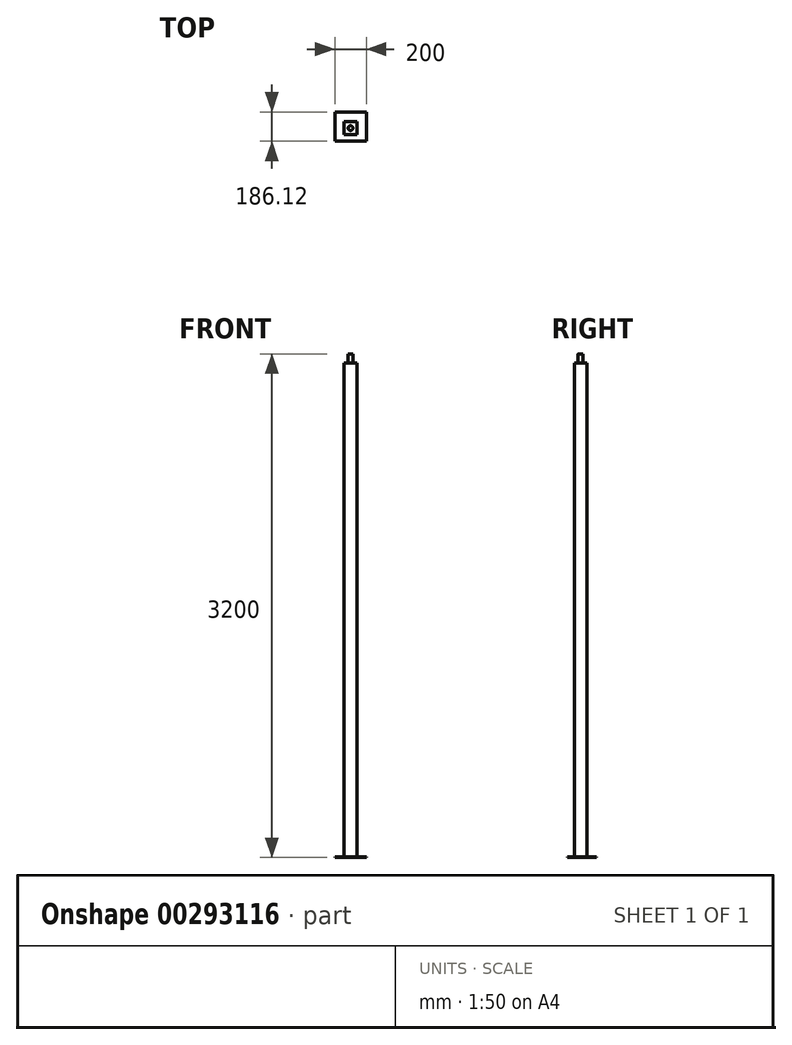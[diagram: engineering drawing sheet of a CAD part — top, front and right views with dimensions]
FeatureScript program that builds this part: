
annotation { "Feature Type Name" : "Feature", "Feature Type Description" : "" }
export const myFeature = defineFeature(function(context is Context, id is Id, definition is map)
    precondition{}
    {
        {
            var Q0;
            Q0=qCreatedBy(makeId("Top.planeOp"),FACE);
            var sketch = newSketch(context, id + "F0", { "sketchPlane" : qUnion([Q0])});
            skLineSegment(sketch, "E0.bottom", {"start": v(100, -93.06) * mm, "end": v(-100, -93.06) * mm});
            skLineSegment(sketch, "E0.top", {"start": v(100, 93.06) * mm, "end": v(-100, 93.06) * mm});
            skLineSegment(sketch, "E0.left", {"start": v(100, -93.06) * mm, "end": v(100, 93.06) * mm});
            skLineSegment(sketch, "E0.right", {"start": v(-100, -93.06) * mm, "end": v(-100, 93.06) * mm});
            skPoint(sketch, "E0.middle", {"position": v(0, 0) * mm});
            skSolve(sketch);
        }
        {
            var Q0;
            Q0=makeQuery(id+"F0.imprint","IMPRINT",FACE,{"disambiguationData":[TD([[makeQuery(id+"F0.imprint","IMPRINT",EDGE,{"derivedFrom":sQuery(id+"F0.wireOp",EDGE,"E0.bottom")}),-1.0]])]});
            extrude(context, id + "F1", {"entities" : qUnion([Q0]), "depth" : 3 * mm});
        }
        {
            var Q0;
            Q0=makeQuery(id+"F1.opExtrude","CAP_FACE",FACE,{"disambiguationData":[OSD([sQuery(id+"F0.wireOp",EDGE,"E0.bottom"),sQuery(id+"F0.wireOp",EDGE,"E0.top"),sQuery(id+"F0.wireOp",EDGE,"E0.left"),sQuery(id+"F0.wireOp",EDGE,"E0.right")])],"isStart":false});
            var sketch = newSketch(context, id + "F2", { "sketchPlane" : qUnion([Q0])});
            skLineSegment(sketch, "E1.bottom", {"start": v(40, -49.32) * mm, "end": v(-40, -49.32) * mm});
            skLineSegment(sketch, "E1.top", {"start": v(40, 30.68) * mm, "end": v(-40, 30.68) * mm});
            skLineSegment(sketch, "E1.left", {"start": v(40, -49.32) * mm, "end": v(40, 30.68) * mm});
            skLineSegment(sketch, "E1.right", {"start": v(-40, -49.32) * mm, "end": v(-40, 30.68) * mm});
            skPoint(sketch, "E1.middle", {"position": v(0, -9.32) * mm});
            skSolve(sketch);
        }
        {
            var Q0;
            Q0=makeQuery(id+"F2.imprint","IMPRINT",FACE,{"disambiguationData":[TD([[makeQuery(id+"F2.imprint","IMPRINT",EDGE,{"derivedFrom":sQuery(id+"F2.wireOp",EDGE,"E1.bottom")}),-1.0]])]});
            extrude(context, id + "F3", {"entities" : qUnion([Q0]), "operationType" : NewBodyOperationType.ADD, "depth" : 3197 * mm});
        }
        {
            var Q0;
            Q0=makeQuery(id+"F3.opExtrude","CAP_FACE",FACE,{"disambiguationData":[OSD([sQuery(id+"F2.wireOp",EDGE,"E1.bottom"),sQuery(id+"F2.wireOp",EDGE,"E1.top"),sQuery(id+"F2.wireOp",EDGE,"E1.left"),sQuery(id+"F2.wireOp",EDGE,"E1.right")])],"isStart":false});
            var sketch = newSketch(context, id + "F4", { "sketchPlane" : qUnion([Q0])});
            skCircle(sketch, "E2", {"center": v(0, -9.32) * mm, "radius": 15 * mm});
            skPoint(sketch, "E2.centerSnap0", {"position": v(40, -9.32) * mm});
            skSolve(sketch);
        }
        {
            var Q0;
            Q0=makeQuery(id+"F4.imprint","IMPRINT",FACE,{"disambiguationData":[TD([[makeQuery(id+"F4.imprint","IMPRINT",EDGE,{"derivedFrom":sQuery(id+"F4.wireOp",EDGE,"E2")}),-1.0]])]});
            extrude(context, id + "F5", {"entities" : qUnion([Q0]), "operationType" : NewBodyOperationType.REMOVE, "oppositeDirection" : true, "depth" : 60 * mm});
        }
    });
